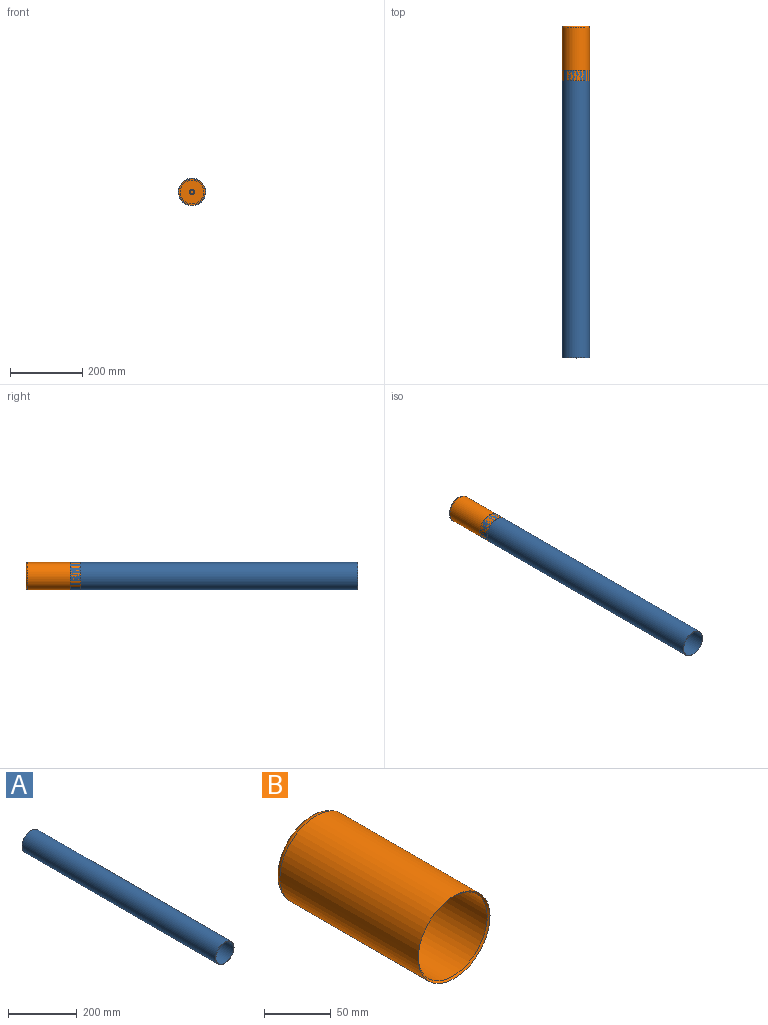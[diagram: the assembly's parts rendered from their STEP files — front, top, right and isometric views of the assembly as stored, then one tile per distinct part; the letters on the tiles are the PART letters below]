
ASSEMBLY  parts=2 mates=1
PART A: 4 faces, bbox 76x798.5x76 mm
  f0: cylinder r=36.5mm len=798.5mm, axis (0,1,0), area 183125mm2, adj f2,f3
  f1: cylinder r=38mm len=797mm, axis (0,1,0), area 190292.6mm2, adj f2,f3
  f2: plane 76x76mm, normal (0,-1,0), area 351.1mm2, adj f0,f1
  f3: cone r=38mm half-angle=45deg, axis (0,-1,0), area 496.5mm2, adj f0,f1
PART B: 10 faces, bbox 82.3x151.5x82.3 mm
  f0: plane 73x73mm, normal (0,-1,0), area 4052.7mm2, adj f3,f5
  f1: cylinder r=38mm len=146.5mm, axis (0,-1,0), area 34978.5mm2, adj f8,f9
  f2: plane 66x66mm, normal (0,1,0), area 3421.2mm2, adj f8
  f3: cylinder r=36.5mm len=147mm, axis (0,1,0), area 33712.4mm2, adj f0,f9
  f4: cylinder r=5mm len=10mm, axis (0,1,0), area 157.1mm2, adj f6,f7
  f5: cylinder r=6.5mm len=13mm, axis (0,1,0), area 204.2mm2, adj f0,f6
  f6: plane 13x13mm, normal (0,-1,0), area 54.2mm2, adj f4,f5
  f7: plane 10x10mm, normal (0,-1,0), area 78.5mm2, adj f4
  f8: torus R=33mm, axis (0,-1,0), area 1785.6mm2, adj f1,f2
  f9: cone r=36.5mm half-angle=45deg, axis (0,-1,0), area 496.5mm2, adj f1,f3
PLACE A t=(-236.23,163.96,-150.61)mm
PLACE B t=(-236.23,280.96,-150.61)mm
MATE planar B.f3 <-> A.f1  axis (0,-1,0) through (-236.23,132.46,-150.61)mm
